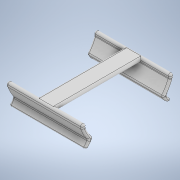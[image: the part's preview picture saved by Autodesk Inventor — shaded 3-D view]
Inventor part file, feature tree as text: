
AUTODESK INVENTOR PART (.ipt)
format: ipt  version: 2020 (Build 240168000, 168)  size: 371,200 bytes
history: native  units: in
note: dims shown in document units (in); Inventor stores cm internally (conversion verified against a paired STEP export)
features: fillet x4, extrude x3, sketch x3
ambient origin geometry x8: Origin, YZ Plane, XZ Plane, XY Plane, X Axis, Y Axis, Z Axis, Center Point
bodies: Solid1 (feature_tree)
feature tree (10):
  extrude  "Extrusion1"  Depth=0.7874in
  extrude  "Extrusion2"  Depth=0.1969in
  fillet  "Fillet1"  Radius=0.1181in
  fillet  "Fillet2"  Radius=0.1181in
  fillet  "Fillet3"  Radius=0.1181in
  extrude  "Extrusion3"  Depth=0.3937in
  fillet  "Fillet5"  Radius=0.3937in
  sketch  "Sketch1"  dims[d0=2.5591in d1=0.7874in]
  sketch  "Sketch2"  dims[d2=0.1969in d3=0.1969in d4=0.1181in d5=0.1181in d6=0.1181in]
  sketch  "Sketch3"  dims[d7=0.1575in d8=0.3937in d9=0.3937in d10=0.1181in d11=0.1181in d12=0.3937in d13=0.3937in d14=2.3622in d15=0.0in d16=0.2756in d17=0.1181in d18=0.1181in d19=0.1181in d20=0.1181in d21=0.5512in d22=0.1181in d23=0.0in d24=0.0591in d25=0.0591in d26=0.0591in d28=0.0394in d29=3.0in d30=0.0in d31=0.0197in]
